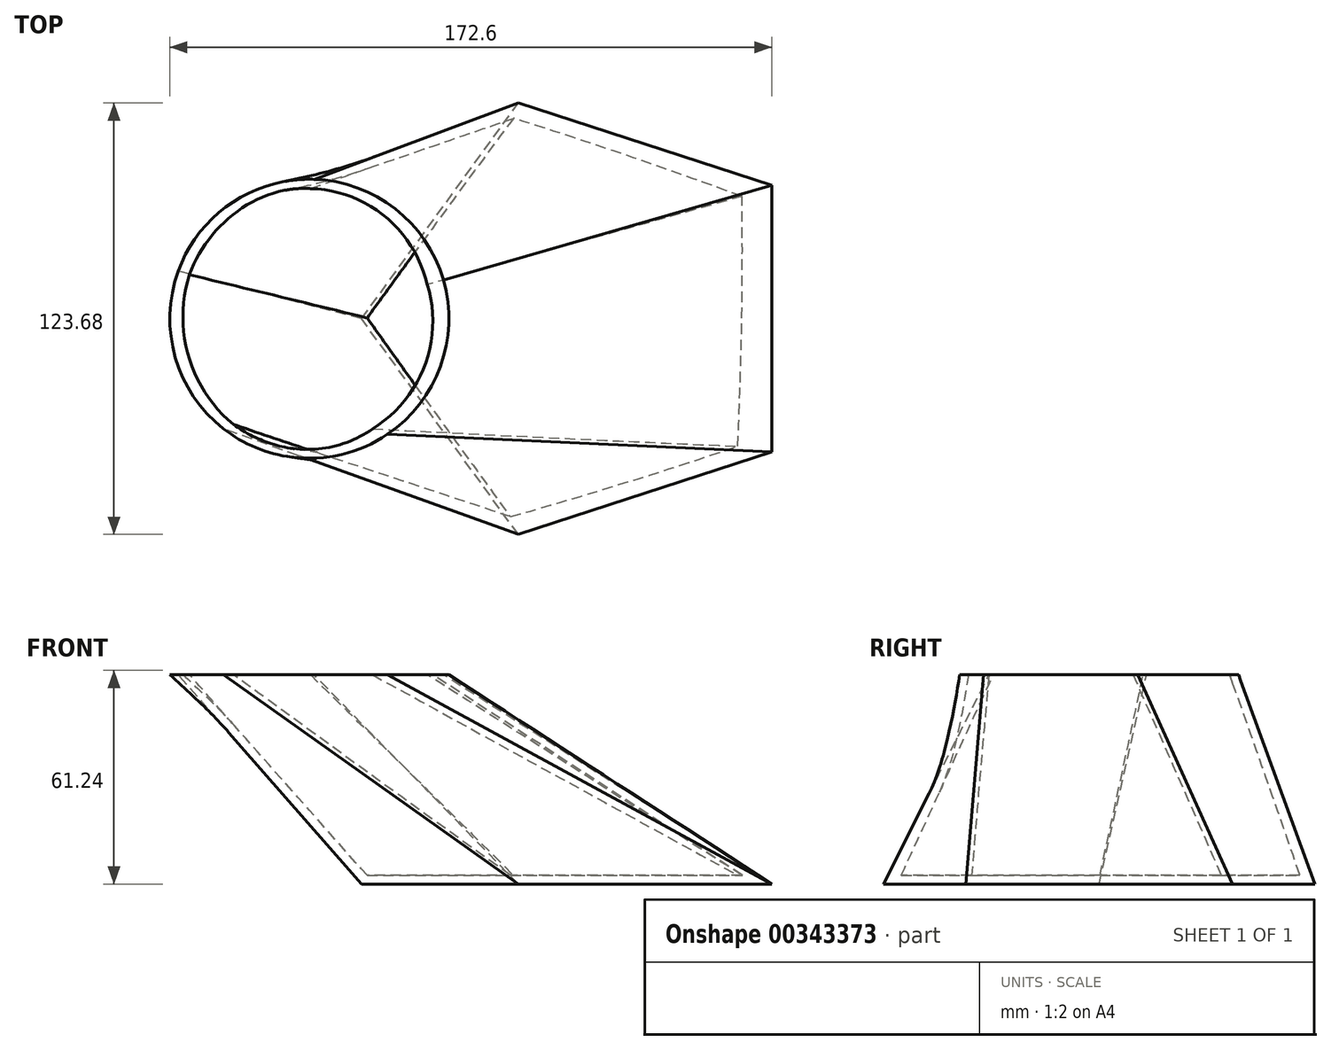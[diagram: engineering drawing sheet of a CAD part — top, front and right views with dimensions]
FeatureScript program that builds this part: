
annotation { "Feature Type Name" : "Feature", "Feature Type Description" : "" }
export const myFeature = defineFeature(function(context is Context, id is Id, definition is map)
    precondition{}
    {
        {
            var Q0;
            Q0=qCreatedBy(makeId("Top.planeOp"),FACE);
            var sketch = newSketch(context, id + "F0", { "sketchPlane" : qUnion([Q0])});
            skCircle(sketch, "E0.cCircle", {"center": v(0, 0) * mm, "radius": 52.6 * mm, "construction": true});
            skLineSegment(sketch, "E0.0", {"start": v(52.6, 38.22) * mm, "end": v(52.6, -38.22) * mm});
            skLineSegment(sketch, "E0.1", {"start": v(52.6, -38.22) * mm, "end": v(-20.1, -61.84) * mm});
            skLineSegment(sketch, "E0.2", {"start": v(-20.1, -61.84) * mm, "end": v(-65.02, 0) * mm});
            skLineSegment(sketch, "E0.3", {"start": v(-65.02, 0) * mm, "end": v(-20.1, 61.84) * mm});
            skLineSegment(sketch, "E0.4", {"start": v(-20.1, 61.84) * mm, "end": v(52.6, 38.22) * mm});
            skPoint(sketch, "E0.0.midPoint", {"position": v(52.6, 0) * mm});
            skSolve(sketch);
        }
        {
            var Q0;
            Q0=makeQuery(id+"F0.imprint","IMPRINT",FACE,{"disambiguationData":[TD([[makeQuery(id+"F0.imprint","IMPRINT",EDGE,{"derivedFrom":sQuery(id+"F0.wireOp",EDGE,"E0.0")}),-1.0]])]});
            cPlane(context, id + "F1", {"entities" : qUnion([Q0]), "cplaneType" : CPlaneType.OFFSET, "offset" : 60 * mm, "width" : 150 * mm, "height" : 150 * mm});
        }
        {
            var Q0;
            Q0=qCreatedBy(id+"F1.planeOp",FACE);
            var sketch = newSketch(context, id + "F2", { "sketchPlane" : qUnion([Q0])});
            skLineSegment(sketch, "E1", {"start": v(0, 0) * mm, "end": v(-80, 0) * mm, "construction": true});
            skCircle(sketch, "E2", {"center": v(-80, 0) * mm, "radius": 40 * mm});
            skSolve(sketch);
        }
        {
            var Q0;
            Q0=makeQuery(id+"F0.imprint","IMPRINT",FACE,{"disambiguationData":[TD([[makeQuery(id+"F0.imprint","IMPRINT",EDGE,{"derivedFrom":sQuery(id+"F0.wireOp",EDGE,"E0.0")}),-1.0]])]});
            var Q1;
            Q1=makeQuery(id+"F2.imprint","IMPRINT",FACE,{"disambiguationData":[TD([[makeQuery(id+"F2.imprint","IMPRINT",EDGE,{"derivedFrom":sQuery(id+"F2.wireOp",EDGE,"E2")}),1.0]])]});
            loft(context, id + "F3", {"sheetProfilesArray" : [{ "sheetProfileEntities" : qUnion([Q0]) }, { "sheetProfileEntities" : qUnion([Q1]) }]});
        }
        {
            var Q0;
            Q0=makeQuery(id+"F3.opLoft","CAP_FACE",FACE,{"disambiguationData":[OSD([makeQuery(id+"F2.imprint","IMPRINT",FACE,{"disambiguationData":[TD([[makeQuery(id+"F2.imprint","IMPRINT",EDGE,{"derivedFrom":sQuery(id+"F2.wireOp",EDGE,"E2")}),1.0]])]})])],"isStart":true});
            shell(context, id + "F4", {"entities" : qUnion([Q0]), "thickness" : 2.5 * mm});
        }
    });
